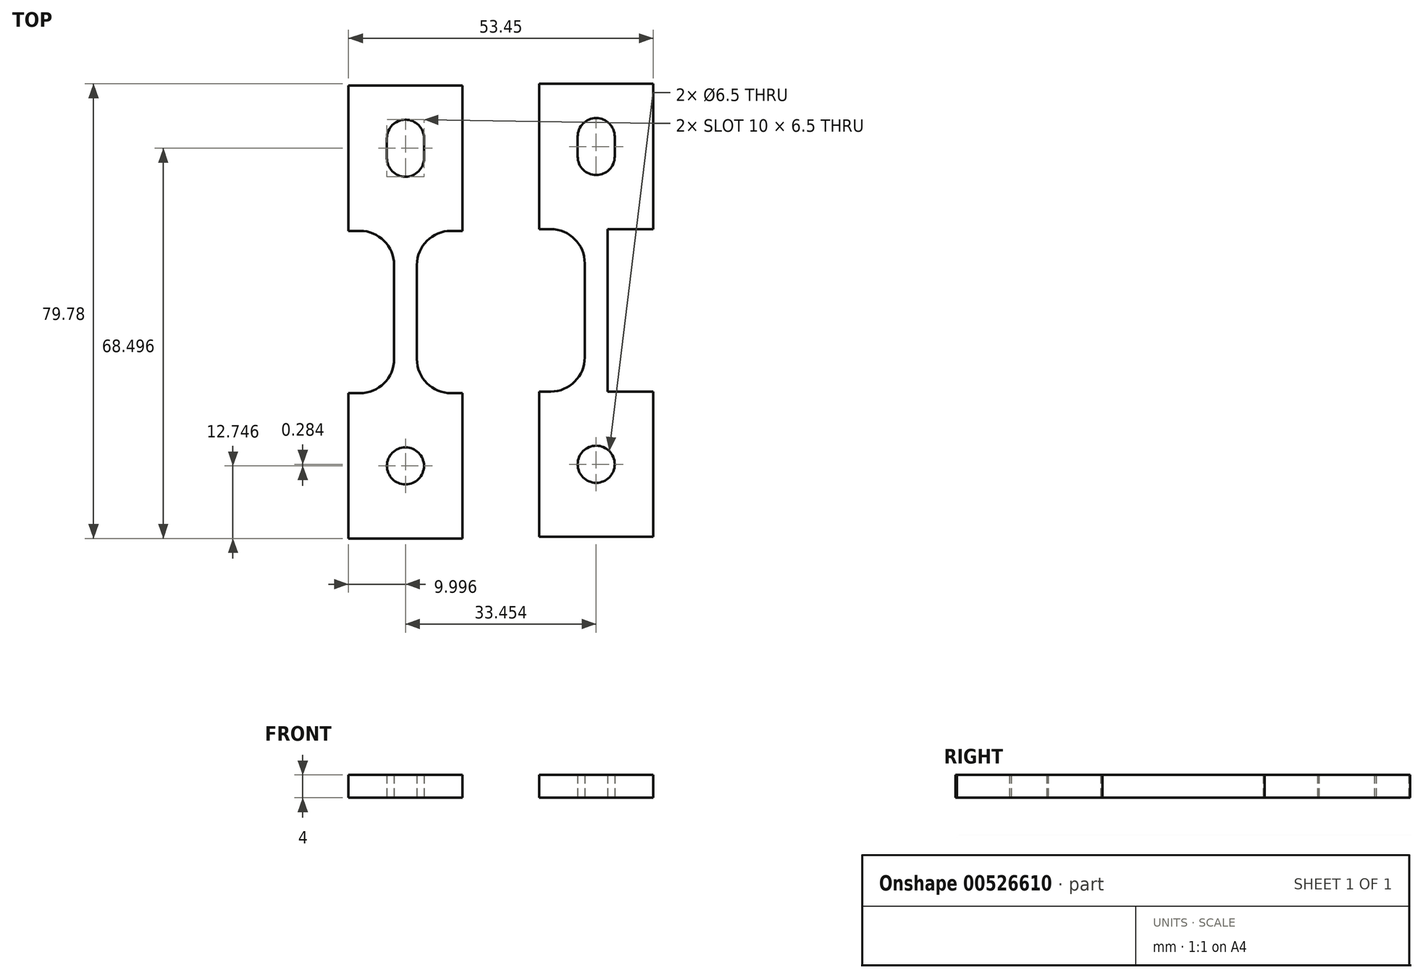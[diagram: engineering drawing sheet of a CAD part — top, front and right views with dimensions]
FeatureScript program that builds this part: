
annotation { "Feature Type Name" : "Feature", "Feature Type Description" : "" }
export const myFeature = defineFeature(function(context is Context, id is Id, definition is map)
    precondition{}
    {
        {
            var Q0;
            Q0=qCreatedBy(makeId("Top.planeOp"),FACE);
            var sketch = newSketch(context, id + "F0", { "sketchPlane" : qUnion([Q0])});
            skLineSegment(sketch, "E0.bottom", {"start": v(-10, 39.75) * mm, "end": v(10, 39.75) * mm});
            skLineSegment(sketch, "E0.top", {"start": v(-10, 14.25) * mm, "end": v(10, 14.25) * mm});
            skLineSegment(sketch, "E0.left", {"start": v(-10, 39.75) * mm, "end": v(-10, 14.25) * mm});
            skLineSegment(sketch, "E0.right", {"start": v(10, 39.75) * mm, "end": v(10, 14.25) * mm});
            skLineSegment(sketch, "E1", {"start": v(0, 30.5) * mm, "end": v(0, 27) * mm, "construction": true});
            skPoint(sketch, "E1.endSnap0", {"position": v(0, 28.75) * mm});
            skArc(sketch, "E2.0.startCap", {"start": v(-3.25, 30.5) * mm, "mid": v(0, 33.75) * mm, "end": v(3.25, 30.5) * mm});
            skArc(sketch, "E2.0.endCap", {"start": v(3.25, 27) * mm, "mid": v(0, 23.75) * mm, "end": v(-3.25, 27) * mm});
            skLineSegment(sketch, "E2.0.left", {"start": v(3.25, 30.5) * mm, "end": v(3.25, 27) * mm});
            skLineSegment(sketch, "E2.0.right", {"start": v(-3.25, 30.5) * mm, "end": v(-3.25, 27) * mm});
            skCircle(sketch, "E3", {"center": v(0, -27) * mm, "radius": 3.25 * mm});
            skLineSegment(sketch, "E4.bottom", {"start": v(-10, -39.75) * mm, "end": v(10, -39.75) * mm});
            skLineSegment(sketch, "E4.top", {"start": v(-10, -14.25) * mm, "end": v(10, -14.25) * mm});
            skLineSegment(sketch, "E4.left", {"start": v(-10, -39.75) * mm, "end": v(-10, -14.25) * mm});
            skLineSegment(sketch, "E4.right", {"start": v(10, -39.75) * mm, "end": v(10, -14.25) * mm});
            skLineSegment(sketch, "E5", {"start": v(-10, -39.75) * mm, "end": v(10, -14.25) * mm, "construction": true});
            skLineSegment(sketch, "E6", {"start": v(0, 23.75) * mm, "end": v(0, 0) * mm, "construction": true});
            skLineSegment(sketch, "E7", {"start": v(0, 0) * mm, "end": v(0, -23.75) * mm, "construction": true});
            skLineSegment(sketch, "E8", {"start": v(0, 23.75) * mm, "end": v(-10, 23.75) * mm, "construction": true});
            skLineSegment(sketch, "E9", {"start": v(-10, 23.75) * mm, "end": v(-10, 14.25) * mm, "construction": true});
            skLineSegment(sketch, "E10", {"start": v(0, -23.75) * mm, "end": v(-10, -23.75) * mm, "construction": true});
            skLineSegment(sketch, "E11", {"start": v(-10, -23.75) * mm, "end": v(-10, -14.25) * mm, "construction": true});
            skLineSegment(sketch, "E12.bottom", {"start": v(-43.45, 39.47) * mm, "end": v(-23.45, 39.47) * mm});
            skLineSegment(sketch, "E12.top", {"start": v(-43.45, 13.97) * mm, "end": v(-23.45, 13.97) * mm});
            skLineSegment(sketch, "E12.left", {"start": v(-43.45, 39.47) * mm, "end": v(-43.45, 13.97) * mm});
            skLineSegment(sketch, "E12.right", {"start": v(-23.45, 39.47) * mm, "end": v(-23.45, 13.97) * mm});
            skLineSegment(sketch, "E13", {"start": v(-33.45, 30.22) * mm, "end": v(-33.45, 26.72) * mm, "construction": true});
            skPoint(sketch, "E13.endSnap0", {"position": v(-33.45, 28.47) * mm});
            skArc(sketch, "E14.0.startCap", {"start": v(-36.7, 30.22) * mm, "mid": v(-33.45, 33.47) * mm, "end": v(-30.2, 30.22) * mm});
            skArc(sketch, "E14.0.endCap", {"start": v(-30.2, 26.72) * mm, "mid": v(-33.45, 23.47) * mm, "end": v(-36.7, 26.72) * mm});
            skLineSegment(sketch, "E14.0.left", {"start": v(-30.2, 30.22) * mm, "end": v(-30.2, 26.72) * mm});
            skLineSegment(sketch, "E14.0.right", {"start": v(-36.7, 30.22) * mm, "end": v(-36.7, 26.72) * mm});
            skCircle(sketch, "E15", {"center": v(-33.45, -27.28) * mm, "radius": 3.25 * mm});
            skLineSegment(sketch, "E16.bottom", {"start": v(-43.45, -40.03) * mm, "end": v(-23.45, -40.03) * mm});
            skLineSegment(sketch, "E16.top", {"start": v(-43.45, -14.53) * mm, "end": v(-23.45, -14.53) * mm});
            skLineSegment(sketch, "E16.left", {"start": v(-43.45, -40.03) * mm, "end": v(-43.45, -14.53) * mm});
            skLineSegment(sketch, "E16.right", {"start": v(-23.45, -40.03) * mm, "end": v(-23.45, -14.53) * mm});
            skLineSegment(sketch, "E17", {"start": v(-43.45, -40.03) * mm, "end": v(-23.45, -14.53) * mm, "construction": true});
            skLineSegment(sketch, "E18", {"start": v(-33.45, 23.47) * mm, "end": v(-33.45, -0.28) * mm, "construction": true});
            skLineSegment(sketch, "E19", {"start": v(-33.45, -0.28) * mm, "end": v(-33.45, -24.03) * mm, "construction": true});
            skLineSegment(sketch, "E20", {"start": v(-33.45, 23.47) * mm, "end": v(-43.45, 23.47) * mm, "construction": true});
            skLineSegment(sketch, "E21", {"start": v(-43.45, 23.47) * mm, "end": v(-43.45, 13.97) * mm, "construction": true});
            skLineSegment(sketch, "E22", {"start": v(-33.45, -24.03) * mm, "end": v(-43.45, -24.03) * mm, "construction": true});
            skLineSegment(sketch, "E23", {"start": v(-43.45, -24.03) * mm, "end": v(-43.45, -14.53) * mm, "construction": true});
            skLineSegment(sketch, "E24.bottom", {"start": v(-35.45, 13.97) * mm, "end": v(-31.45, 13.97) * mm});
            skLineSegment(sketch, "E24.top", {"start": v(-35.45, -14.53) * mm, "end": v(-31.45, -14.53) * mm});
            skLineSegment(sketch, "E24.left", {"start": v(-35.45, 13.97) * mm, "end": v(-35.45, -14.53) * mm});
            skLineSegment(sketch, "E24.right", {"start": v(-31.45, 13.97) * mm, "end": v(-31.45, -14.53) * mm});
            skLineSegment(sketch, "E25", {"start": v(-33.45, 13.97) * mm, "end": v(-33.45, -14.53) * mm, "construction": true});
            skSolve(sketch);
        }
        {
            var Q0;
            Q0=qSketchRegion(id+"F0",true);
            extrude(context, id + "F1", {"entities" : qUnion([Q0]), "depth" : 4 * mm, "offsetDistance" : 25 * mm});
        }
        {
            var Q0;
            Q0=qCreatedBy(makeId("Top.planeOp"),FACE);
            var sketch = newSketch(context, id + "F2", { "sketchPlane" : qUnion([Q0])});
            skLineSegment(sketch, "E26.bottom", {"start": v(-2, 14.25) * mm, "end": v(2, 14.25) * mm});
            skLineSegment(sketch, "E26.top", {"start": v(-2, -14.25) * mm, "end": v(2, -14.25) * mm});
            skLineSegment(sketch, "E26.left", {"start": v(-2, 14.25) * mm, "end": v(-2, -14.25) * mm});
            skLineSegment(sketch, "E26.right", {"start": v(2, 14.25) * mm, "end": v(2, -14.25) * mm});
            skLineSegment(sketch, "E27", {"start": v(0, 14.25) * mm, "end": v(0, -14.25) * mm, "construction": true});
            skSolve(sketch);
        }
        {
            var Q0;
            Q0=qSketchRegion(id+"F2",true);
            extrude(context, id + "F3", {"entities" : qUnion([Q0]), "operationType" : NewBodyOperationType.ADD, "depth" : 4 * mm});
        }
        {
            var Q0;
            Q0=makeQuery(id+"F3.opExtrude","SWEPT_EDGE",EDGE,{"disambiguationData":[OSD([sQuery(id+"F2.wireOp",EDGE,"E26.bottom"),sQuery(id+"F2.wireOp",EDGE,"E26.left")])]});
            var Q1;
            Q1=makeQuery(id+"F3.opExtrude","SWEPT_EDGE",EDGE,{"disambiguationData":[OSD([sQuery(id+"F2.wireOp",EDGE,"E26.bottom"),sQuery(id+"F2.wireOp",EDGE,"E26.right")])]});
            var Q2;
            Q2=makeQuery(id+"F3.opExtrude","SWEPT_EDGE",EDGE,{"disambiguationData":[OSD([sQuery(id+"F2.wireOp",EDGE,"E26.top"),sQuery(id+"F2.wireOp",EDGE,"E26.right")])]});
            var Q3;
            Q3=makeQuery(id+"F3.opExtrude","SWEPT_EDGE",EDGE,{"disambiguationData":[OSD([sQuery(id+"F2.wireOp",EDGE,"E26.top"),sQuery(id+"F2.wireOp",EDGE,"E26.left")])]});
            var Q4;
            Q4=makeQuery(id+"F1.opExtrude","SWEPT_EDGE",EDGE,{"disambiguationData":[OSD([sQuery(id+"F0.wireOp",EDGE,"E12.top"),sQuery(id+"F0.wireOp",EDGE,"E24.bottom"),sQuery(id+"F0.wireOp",EDGE,"E24.left")])]});
            var Q5;
            Q5=makeQuery(id+"F1.opExtrude","SWEPT_EDGE",EDGE,{"disambiguationData":[OSD([sQuery(id+"F0.wireOp",EDGE,"E12.top"),sQuery(id+"F0.wireOp",EDGE,"E24.bottom"),sQuery(id+"F0.wireOp",EDGE,"E24.right")])]});
            var Q6;
            Q6=makeQuery(id+"F1.opExtrude","SWEPT_EDGE",EDGE,{"disambiguationData":[OSD([sQuery(id+"F0.wireOp",EDGE,"E16.top"),sQuery(id+"F0.wireOp",EDGE,"E24.top"),sQuery(id+"F0.wireOp",EDGE,"E24.right")])]});
            var Q7;
            Q7=makeQuery(id+"F1.opExtrude","SWEPT_EDGE",EDGE,{"disambiguationData":[OSD([sQuery(id+"F0.wireOp",EDGE,"E16.top"),sQuery(id+"F0.wireOp",EDGE,"E24.top"),sQuery(id+"F0.wireOp",EDGE,"E24.left")])]});
            fillet(context, id + "F4", {"entities" : qUnion([Q0, Q1, Q2, Q3, Q4, Q5, Q6, Q7]), "radius" : 6 * mm, "tangentPropagation" : true, "allowEdgeOverflow" : false});
        }
    });
